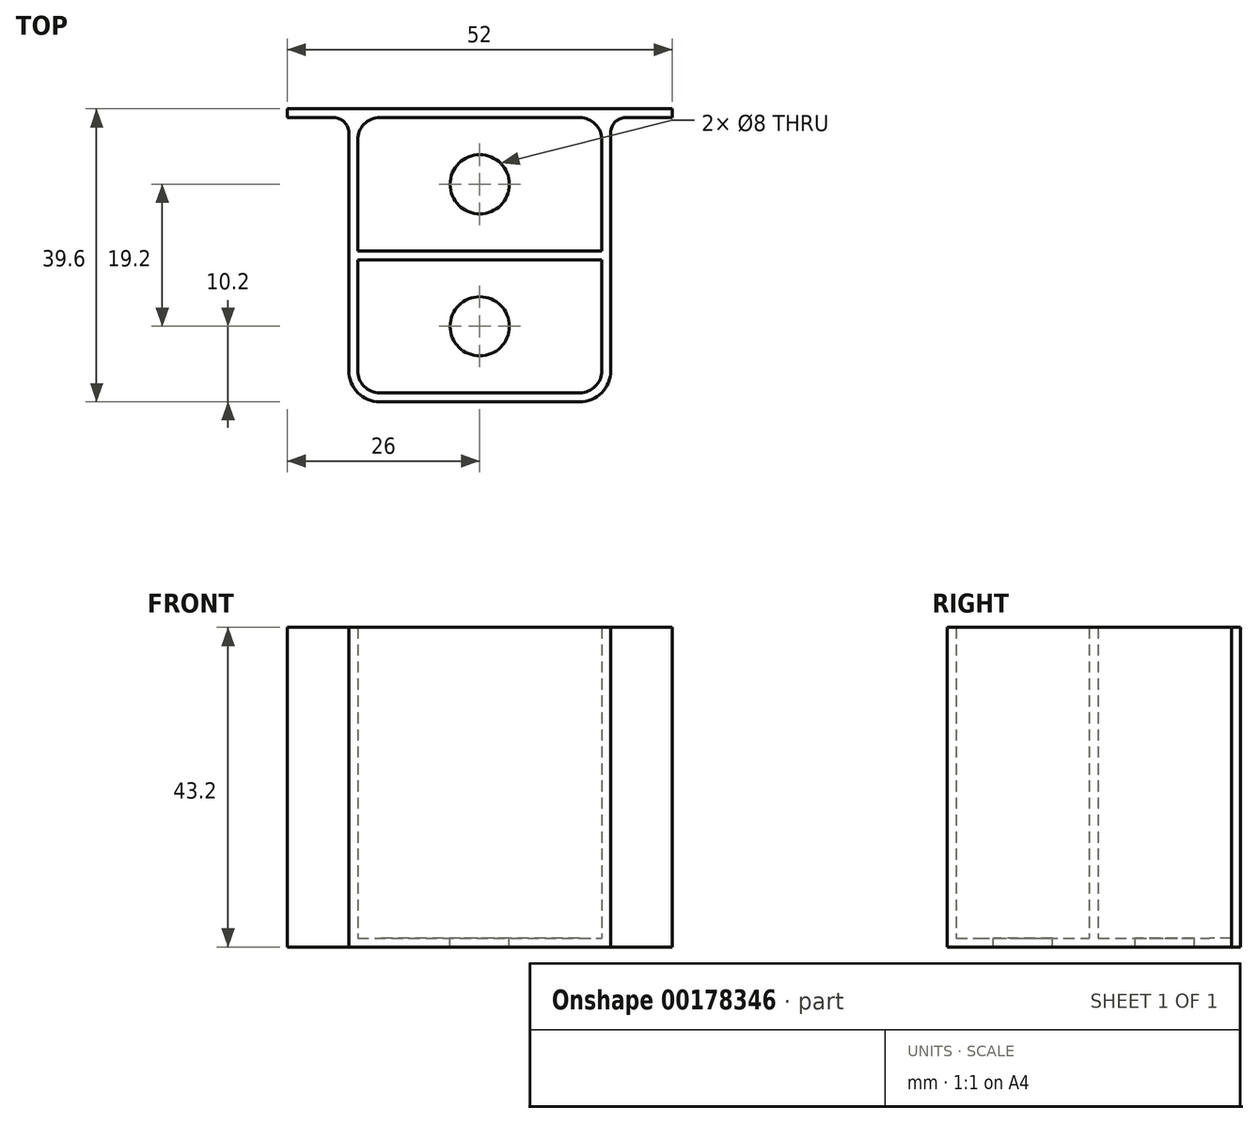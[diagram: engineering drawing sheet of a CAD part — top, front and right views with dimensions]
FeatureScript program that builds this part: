
annotation { "Feature Type Name" : "Feature", "Feature Type Description" : "" }
export const myFeature = defineFeature(function(context is Context, id is Id, definition is map)
    precondition{}
    {
        {
            var Q0;
            Q0=qCreatedBy(makeId("Top.planeOp"),FACE);
            var sketch = newSketch(context, id + "F0", { "sketchPlane" : qUnion([Q0])});
            skLineSegment(sketch, "E0.bottom", {"start": v(13.5, -18.6) * mm, "end": v(-13.5, -18.6) * mm});
            skLineSegment(sketch, "E0.top", {"start": v(13.5, 18.6) * mm, "end": v(-13.5, 18.6) * mm});
            skLineSegment(sketch, "E0.left", {"start": v(16.5, -15.6) * mm, "end": v(16.5, 15.6) * mm});
            skLineSegment(sketch, "E0.right", {"start": v(-16.5, -15.6) * mm, "end": v(-16.5, 15.6) * mm});
            skPoint(sketch, "E0.middle", {"position": v(0, 0) * mm});
            skLineSegment(sketch, "E1", {"start": v(-16.5, -0.6) * mm, "end": v(16.5, -0.6) * mm});
            skLineSegment(sketch, "E2", {"start": v(-16.5, 0.6) * mm, "end": v(16.5, 0.6) * mm});
            skCircle(sketch, "E3", {"center": v(0, 9.6) * mm, "radius": 4 * mm});
            skPoint(sketch, "E3.centerSnap0", {"position": v(0, 0.6) * mm});
            skCircle(sketch, "E4", {"center": v(0, -9.6) * mm, "radius": 4 * mm});
            skLineSegment(sketch, "E5", {"start": v(0, 0.6) * mm, "end": v(0, 18.6) * mm, "construction": true});
            skLineSegment(sketch, "E6", {"start": v(0, -0.6) * mm, "end": v(0, -18.6) * mm, "construction": true});
            skPoint(sketch, "E7.visualSharp", {"position": v(-16.5, 18.6) * mm});
            skArc(sketch, "E7.filletArc", {"start": v(-13.5, 18.6) * mm, "mid": v(-15.62, 17.72) * mm, "end": v(-16.5, 15.6) * mm});
            skPoint(sketch, "E8.visualSharp", {"position": v(16.5, 18.6) * mm});
            skArc(sketch, "E8.filletArc", {"start": v(16.5, 15.6) * mm, "mid": v(15.62, 17.72) * mm, "end": v(13.5, 18.6) * mm});
            skPoint(sketch, "E9.visualSharp", {"position": v(16.5, -18.6) * mm});
            skArc(sketch, "E9.filletArc", {"start": v(13.5, -18.6) * mm, "mid": v(15.62, -17.72) * mm, "end": v(16.5, -15.6) * mm});
            skPoint(sketch, "E10.visualSharp", {"position": v(-16.5, -18.6) * mm});
            skArc(sketch, "E10.filletArc", {"start": v(-16.5, -15.6) * mm, "mid": v(-15.62, -17.72) * mm, "end": v(-13.5, -18.6) * mm});
            skLineSegment(sketch, "E11.0", {"start": v(-17.7, -15.6) * mm, "end": v(-17.7, 15.6) * mm});
            skLineSegment(sketch, "E11.1", {"start": v(17.7, -15.6) * mm, "end": v(17.7, 15.6) * mm});
            skArc(sketch, "E11.2", {"start": v(13.5, -19.8) * mm, "mid": v(16.47, -18.57) * mm, "end": v(17.7, -15.6) * mm});
            skLineSegment(sketch, "E11.3", {"start": v(13.5, -19.8) * mm, "end": v(-13.5, -19.8) * mm});
            skArc(sketch, "E11.4", {"start": v(-17.7, -15.6) * mm, "mid": v(-16.47, -18.57) * mm, "end": v(-13.5, -19.8) * mm});
            skLineSegment(sketch, "E12", {"start": v(-26, 19.8) * mm, "end": v(26, 19.8) * mm});
            skPoint(sketch, "E13", {"position": v(0, 19.8) * mm});
            skLineSegment(sketch, "E14", {"start": v(-26, 19.8) * mm, "end": v(-26, 18.6) * mm});
            skLineSegment(sketch, "E15", {"start": v(-26, 18.6) * mm, "end": v(-17.7, 18.6) * mm});
            skLineSegment(sketch, "E16", {"start": v(-17.7, 18.6) * mm, "end": v(-17.7, 15.6) * mm});
            skLineSegment(sketch, "E17", {"start": v(26, 19.8) * mm, "end": v(26, 18.6) * mm});
            skLineSegment(sketch, "E18", {"start": v(26, 18.6) * mm, "end": v(17.7, 18.6) * mm});
            skLineSegment(sketch, "E19", {"start": v(17.7, 18.6) * mm, "end": v(17.7, 15.6) * mm});
            skSolve(sketch);
        }
        {
            var Q0;
            Q0 = qSketchRegion(id + "F0", true);
            var Q1;
            {var subQ0=sQuery(id+"F0.wireOp",EDGE,"E1");Q1=makeQuery(id+"F0.imprint","IMPRINT",FACE,{"disambiguationData":[TD([[makeQuery(id+"F0.imprint","IMPRINT",EDGE,{"derivedFrom":subQ0}),1.0]])]});}
            extrude(context, id + "F1", {"entities" : qUnion([Q0, Q1]), "depth" : 42 * mm, "hasSecondDirection" : true, "secondDirectionOppositeDirection" : true, "secondDirectionDepth" : 1.2 * mm});
        }
        {
            var Q0;
            {var subQ2=sQuery(id+"F0.wireOp",EDGE,"E0.top");Q0=makeQuery(id+"F0.imprint","IMPRINT",FACE,{"disambiguationData":[TD([[makeQuery(id+"F0.imprint","IMPRINT",EDGE,{"derivedFrom":subQ2}),1.0]])]});}
            var Q1;
            {var subQ0=sQuery(id+"F0.wireOp",EDGE,"E1");Q1=makeQuery(id+"F0.imprint","IMPRINT",FACE,{"disambiguationData":[TD([[makeQuery(id+"F0.imprint","IMPRINT",EDGE,{"derivedFrom":subQ0}),1.0]])]});}
            var Q2;
            {var subQ2=sQuery(id+"F0.wireOp",EDGE,"E0.bottom");Q2=makeQuery(id+"F0.imprint","IMPRINT",FACE,{"disambiguationData":[TD([[makeQuery(id+"F0.imprint","IMPRINT",EDGE,{"derivedFrom":subQ2}),-1.0]])]});}
            extrude(context, id + "F2", {"entities" : qUnion([Q0, Q1, Q2]), "operationType" : NewBodyOperationType.ADD, "oppositeDirection" : true, "depth" : 1.2 * mm});
        }
        {
            var Q0;
            Q0=makeQuery(id+"F1.opExtrude","SWEPT_EDGE",EDGE,{"disambiguationData":[OSD([sQuery(id+"F0.wireOp",EDGE,"E15"),sQuery(id+"F0.wireOp",EDGE,"E16")])]});
            var Q1;
            Q1=makeQuery(id+"F1.opExtrude","SWEPT_EDGE",EDGE,{"disambiguationData":[OSD([sQuery(id+"F0.wireOp",EDGE,"E18"),sQuery(id+"F0.wireOp",EDGE,"E19")])]});
            fillet(context, id + "F3", {"entities" : qUnion([Q0, Q1]), "radius" : 2 * mm, "tangentPropagation" : true, "allowEdgeOverflow" : false});
        }
    });
